FCSTD DOCUMENT  (FreeCAD 1.0R39109 (Git))
Label: base_platform
License: All rights reserved
LicenseURL: https://en.wikipedia.org/wiki/All_rights_reserved
objects: App::Link×27, App::FeaturePython×27, Assembly::JointGroup×1, Assembly::AssemblyObject×1
EXTERNAL_REF file=../parts_library/profile_40_serie.FCStd obj=Body001
EXTERNAL_REF file=../parts_library/profile_40_serie.FCStd obj=Body002
EXTERNAL_REF file=../parts_library/corner_bracket_40x40.FCStd obj=Part__Feature
EXTERNAL_REF file=../parts_library/profile_40_serie.FCStd obj=Body004

FEATURE [App::Link] profile_40x160x1350  label="profile_40x160x1350_right"
  LinkPlacement = pos=(605.692,0.000163098,162.079) rot=(0.57735,-0.57735,-0.57735;4.18879rad)
  LinkedObject = -> <external ../parts_library/profile_40_serie.FCStd>#Body001
  Placement = pos=(605.692,0.000163098,162.079) rot=(0.57735,-0.57735,-0.57735;4.18879rad)
FEATURE [App::Link] profile_40x160x1351  label="profile_40x160x1350_left"
  LinkPlacement = pos=(65.6922,3.43521e-05,162.079) rot=(0.57735,-0.57735,-0.57735;4.18879rad)
  LinkedObject = -> <external ../parts_library/profile_40_serie.FCStd>#Body001
  Placement = pos=(65.6922,3.43521e-05,162.079) rot=(0.57735,-0.57735,-0.57735;4.18879rad)
FEATURE [App::Link] profile_40x160x500  label="profile_40x160x500_front"
  LinkPlacement = pos=(540.393,744.701,-1.22589) rot=(0,-1,0;1.5708rad)
  LinkedObject = -> <external ../parts_library/profile_40_serie.FCStd>#Body002
  Placement = pos=(540.393,744.701,-1.22589) rot=(0,-1,0;1.5708rad)
FEATURE [App::Link] profile_40x160x1352  label="profile_40x160x500_rear"
  LinkPlacement = pos=(540.393,1284.7,-1.22602) rot=(0,-1,0;1.5708rad)
  LinkedObject = -> <external ../parts_library/profile_40_serie.FCStd>#Body002
  Placement = pos=(540.393,1284.7,-1.22602) rot=(0,-1,0;1.5708rad)
FEATURE [App::Link] corner_bracket_40x40  label="corner_bracket_40x40_000"
  LinkPlacement = pos=(-47.0395,846,140.426) rot=(0,0,-1;1.5708rad)
  LinkedObject = -> <external ../parts_library/corner_bracket_40x40.FCStd>#Part__Feature
  Placement = pos=(-47.0395,846,140.426) rot=(0,0,-1;1.5708rad)
FEATURE [App::Link] corner_bracket_40x041  label="corner_bracket_40x40_001"
  LinkPlacement = pos=(-47.0395,846,20.4265) rot=(0,0,-1;1.5708rad)
  LinkedObject = -> <external ../parts_library/corner_bracket_40x40.FCStd>#Part__Feature
  Placement = pos=(-47.0395,846,20.4265) rot=(0,0,-1;1.5708rad)
FEATURE [App::Link] corner_bracket_40x042  label="corner_bracket_40x40_002"
  LinkPlacement = pos=(-47.0396,1274,140.426) rot=(0.707107,0.707107,0;3.14159rad)
  LinkedObject = -> <external ../parts_library/corner_bracket_40x40.FCStd>#Part__Feature
  Placement = pos=(-47.0396,1274,140.426) rot=(0.707107,0.707107,0;3.14159rad)
FEATURE [App::Link] corner_bracket_40x043  label="corner_bracket_40x40_003"
  LinkPlacement = pos=(76.3929,1397.43,20.4263) rot=(0,0,1;3.14159rad)
  LinkedObject = -> <external ../parts_library/corner_bracket_40x40.FCStd>#Part__Feature
  Placement = pos=(76.3929,1397.43,20.4263) rot=(0,0,1;3.14159rad)
FEATURE [App::Link] corner_bracket_40x044  label="corner_bracket_40x40_004"
  LinkPlacement = pos=(504.393,722.568,140.426) rot=(-0.57735,0.57735,0.57735;0rad)
  LinkedObject = -> <external ../parts_library/corner_bracket_40x40.FCStd>#Part__Feature
  Placement = pos=(504.393,722.568,140.426) rot=(-0.57735,0.57735,0.57735;0rad)
FEATURE [App::Link] corner_bracket_40x045  label="corner_bracket_40x40_005"
  LinkPlacement = pos=(504.393,722.567,20.4264) rot=(-0.57735,0.57735,0.57735;0rad)
  LinkedObject = -> <external ../parts_library/corner_bracket_40x40.FCStd>#Part__Feature
  Placement = pos=(504.393,722.567,20.4264) rot=(-0.57735,0.57735,0.57735;0rad)
FEATURE [App::Link] corner_bracket_40x046  label="corner_bracket_40x40_006"
  LinkPlacement = pos=(627.826,1274,140.426) rot=(0,0,1;1.5708rad)
  LinkedObject = -> <external ../parts_library/corner_bracket_40x40.FCStd>#Part__Feature
  Placement = pos=(627.826,1274,140.426) rot=(0,0,1;1.5708rad)
FEATURE [App::Link] corner_bracket_40x047  label="corner_bracket_40x40_007"
  LinkPlacement = pos=(627.826,1274,20.4262) rot=(0,0,1;1.5708rad)
  LinkedObject = -> <external ../parts_library/corner_bracket_40x40.FCStd>#Part__Feature
  Placement = pos=(627.826,1274,20.4262) rot=(0,0,1;1.5708rad)
FEATURE [App::FeaturePython] GroundedJoint  label="GroundedJoint_profile_40x160x1350_left"  # Assembly grounded joint (typed FeaturePython)
  ObjectToGround = -> profile_40x160x1351
  Placement = pos=(65.6922,3.43521e-05,162.079) rot=(0.57735,-0.57735,-0.57735;4.18879rad)
FEATURE [App::FeaturePython] Joint  label="Fixed_profile_40x160x500_rear"  # Assembly joint (typed FeaturePython)
  Activated = true
  AngleMax = 0
  AngleMin = 0
  Detach1 = false
  Detach2 = false
  Distance = 0
  Distance2 = 0
  EnableAngleMax = false
  EnableAngleMin = false
  EnableLengthMax = false
  EnableLengthMin = false
  JointType = 0 (Fixed)
  LengthMax = 0
  LengthMin = 0
  Offset2 = pos=(0,0,0) rot=(0,0,-1;1.5708rad)
  Placement1 = pos=(3.65224,25.2989,1350) rot=(0.707107,0,0.707107;3.14159rad)
  Placement2 = pos=(159.652,65.2989,500) rot=(-0.57735,-0.57735,0.57735;2.0944rad)
  Reference1 = -> Assembly [profile_40x160x1351.Edge427,profile_40x160x1351.Vertex425]
  Reference2 = -> Assembly [profile_40x160x1352.Edge322,profile_40x160x1352.Vertex320]
FEATURE [App::FeaturePython] Joint001  label="Fixed_profile_40x160x1350_right"  # Assembly joint (typed FeaturePython)
  Activated = true
  AngleMax = 0
  AngleMin = 0
  Detach1 = false
  Detach2 = false
  Distance = 0
  Distance2 = 0
  EnableAngleMax = false
  EnableAngleMin = false
  EnableLengthMax = false
  EnableLengthMin = false
  JointType = 0 (Fixed)
  LengthMax = 0
  LengthMin = 0
  Offset2 = pos=(0,0,0) rot=(0,0,1;1.5708rad)
  Placement1 = pos=(159.652,65.2989,0) rot=(-0.707107,0,0.707107;3.14159rad)
  Placement2 = pos=(3.65224,65.2989,1350) rot=(-0.57735,0.57735,0.57735;4.18879rad)
  Reference1 = -> Assembly [profile_40x160x1352.Edge150,profile_40x160x1352.Vertex151]
  Reference2 = -> Assembly [profile_40x160x1350.Edge403,profile_40x160x1350.Vertex402]
FEATURE [App::FeaturePython] Joint002  label="Fixed_profile_40x160x500_front"  # Assembly joint (typed FeaturePython)
  Activated = true
  AngleMax = 0
  AngleMin = 0
  Detach1 = false
  Detach2 = false
  Distance = 0
  Distance2 = 0
  EnableAngleMax = false
  EnableAngleMin = false
  EnableLengthMax = false
  EnableLengthMin = false
  JointType = 0 (Fixed)
  LengthMax = 0
  LengthMin = 0
  Offset1 = pos=(0,-540,0) rot=(0,0,1;0rad)
  Offset2 = pos=(0,0,0) rot=(0,0,1;1.5708rad)
  Placement1 = pos=(159.652,605.299,500) rot=(-0.707107,0,0.707107;3.14159rad)
  Placement2 = pos=(3.65224,25.2989,1350) rot=(0.57735,-0.57735,0.57735;4.18879rad)
  Reference1 = -> Assembly [profile_40x160x500.Edge322,profile_40x160x500.Vertex320]
  Reference2 = -> Assembly [profile_40x160x1351.Edge427,profile_40x160x1351.Vertex425]
FEATURE [App::FeaturePython] Joint003  label="Fixed_corner_bracket_40x40_000"  # Assembly joint (typed FeaturePython)
  Activated = true
  AngleMax = 0
  AngleMin = 0
  Detach1 = false
  Detach2 = false
  Distance = 0
  Distance2 = 0
  EnableAngleMax = false
  EnableAngleMin = false
  EnableLengthMax = false
  EnableLengthMin = false
  JointType = 0 (Fixed)
  LengthMax = 0
  LengthMin = 0
  Offset2 = pos=(0,0,-1) rot=(0,0,1;3.14159rad)
  Placement1 = pos=(159.652,65.2989,500) rot=(0,1,0;3.14159rad)
  Placement2 = pos=(36,87.4326,18) rot=(0.57735,-0.57735,-0.57735;4.18879rad)
  Reference1 = -> Assembly [profile_40x160x500.Edge580,profile_40x160x500.Vertex320]
  Reference2 = -> Assembly [corner_bracket_40x40.Edge44,corner_bracket_40x40.Vertex43]
FEATURE [App::FeaturePython] Joint004  label="Fixed_corner_bracket_40x40_001"  # Assembly joint (typed FeaturePython)
  Activated = true
  AngleMax = 0
  AngleMin = 0
  Detach1 = false
  Detach2 = false
  Distance = 0
  Distance2 = 0
  EnableAngleMax = false
  EnableAngleMin = false
  EnableLengthMax = false
  EnableLengthMin = false
  JointType = 0 (Fixed)
  LengthMax = 0
  LengthMin = 0
  Offset2 = pos=(0,0,-1) rot=(0,0,1;3.14159rad)
  Placement1 = pos=(3.65224,65.2989,500) rot=(0,1,0;3.14159rad)
  Placement2 = pos=(36,87.4326,-18) rot=(0.57735,-0.57735,-0.57735;4.18879rad)
  Reference1 = -> Assembly [profile_40x160x500.Edge661,profile_40x160x500.Vertex401]
  Reference2 = -> Assembly [corner_bracket_40x041.Edge56,corner_bracket_40x041.Vertex54]
FEATURE [App::FeaturePython] Joint005  label="Fixed_corner_bracket_40x40_002"  # Assembly joint (typed FeaturePython)
  Activated = true
  AngleMax = 0
  AngleMin = 0
  Detach1 = false
  Detach2 = false
  Distance = 0
  Distance2 = 0
  EnableAngleMax = false
  EnableAngleMin = false
  EnableLengthMax = false
  EnableLengthMin = false
  JointType = 0 (Fixed)
  LengthMax = 0
  LengthMin = 0
  Offset2 = pos=(0,0,-1) rot=(0,0,1;0rad)
  Placement1 = pos=(159.652,25.2989,500) rot=(0,1,0;3.14159rad)
  Placement2 = pos=(36,87.4326,-18) rot=(0.57735,0.57735,0.57735;4.18879rad)
  Reference1 = -> Assembly [profile_40x160x1352.Edge557,profile_40x160x1352.Vertex297]
  Reference2 = -> Assembly [corner_bracket_40x042.Edge56,corner_bracket_40x042.Vertex54]
FEATURE [App::FeaturePython] Joint006  label="Fixed_corner_bracket_40x40_003"  # Assembly joint (typed FeaturePython)
  Activated = true
  AngleMax = 0
  AngleMin = 0
  Detach1 = false
  Detach2 = false
  Distance = 0
  Distance2 = 0
  EnableAngleMax = false
  EnableAngleMin = false
  EnableLengthMax = false
  EnableLengthMin = false
  JointType = 0 (Fixed)
  LengthMax = 0
  LengthMin = 0
  Offset2 = pos=(0,0,1) rot=(0,0,1;3.14159rad)
  Placement1 = pos=(35,87.4326,-18) rot=(0.707107,0,0.707107;3.14159rad)
  Placement2 = pos=(3.65224,25.2989,499) rot=(1,0,0;3.14159rad)
  Reference1 = -> Assembly [corner_bracket_40x043.Edge22,corner_bracket_40x043.Vertex22]
  Reference2 = -> Assembly [profile_40x160x1352.Edge684,profile_40x160x1352.Vertex424]
FEATURE [App::FeaturePython] Joint007  label="Fixed_corner_bracket_40x40_004"  # Assembly joint (typed FeaturePython)
  Activated = true
  AngleMax = 0
  AngleMin = 0
  Detach1 = false
  Detach2 = false
  Distance = 0
  Distance2 = 0
  EnableAngleMax = false
  EnableAngleMin = false
  EnableLengthMax = false
  EnableLengthMin = false
  JointType = 0 (Fixed)
  LengthMax = 0
  LengthMin = 0
  Offset2 = pos=(0,0,-1) rot=(0,0,1;3.14159rad)
  Placement1 = pos=(35,87.4326,18) rot=(0.707107,0,0.707107;3.14159rad)
  Placement2 = pos=(159.652,65.2989,1) rot=(1,0,0;3.14159rad)
  Reference1 = -> Assembly [corner_bracket_40x044.Edge7,corner_bracket_40x044.Vertex7]
  Reference2 = -> Assembly [profile_40x160x500.Edge580,profile_40x160x500.Vertex151]
FEATURE [App::FeaturePython] Joint008  label="Fixed_corner_bracket_40x40_005"  # Assembly joint (typed FeaturePython)
  Activated = true
  AngleMax = 0
  AngleMin = 0
  Detach1 = false
  Detach2 = false
  Distance = 0
  Distance2 = 0
  EnableAngleMax = false
  EnableAngleMin = false
  EnableLengthMax = false
  EnableLengthMin = false
  JointType = 0 (Fixed)
  LengthMax = 0
  LengthMin = 0
  Offset2 = pos=(0,0,1) rot=(0,0,1;3.14159rad)
  Placement1 = pos=(3.65224,65.2989,0) rot=(0,1,0;3.14159rad)
  Placement2 = pos=(36,87.4326,-18) rot=(0,-1,0;4.71239rad)
  Reference1 = -> Assembly [profile_40x160x500.Edge661,profile_40x160x500.Vertex70]
  Reference2 = -> Assembly [corner_bracket_40x045.Edge22,corner_bracket_40x045.Vertex22]
FEATURE [App::FeaturePython] Joint009  label="Fixed_corner_bracket_40x40_006"  # Assembly joint (typed FeaturePython)
  Activated = true
  AngleMax = 0
  AngleMin = 0
  Detach1 = false
  Detach2 = false
  Distance = 0
  Distance2 = 0
  EnableAngleMax = false
  EnableAngleMin = false
  EnableLengthMax = false
  EnableLengthMin = false
  JointType = 0 (Fixed)
  LengthMax = 0
  LengthMin = 0
  Offset2 = pos=(0,0,-1) rot=(0,0,1;3.14159rad)
  Placement1 = pos=(36,88.4326,18) rot=(0.57735,0.57735,0.57735;4.18879rad)
  Placement2 = pos=(159.652,25.2989,1) rot=(1,0,0;3.14159rad)
  Reference1 = -> Assembly [corner_bracket_40x046.Edge44,corner_bracket_40x046.Vertex43]
  Reference2 = -> Assembly [profile_40x160x1352.Edge557,profile_40x160x1352.Vertex174]
FEATURE [App::FeaturePython] Joint010  label="Fixed_corner_bracket_40x40_007"  # Assembly joint (typed FeaturePython)
  Activated = true
  AngleMax = 0
  AngleMin = 0
  Detach1 = false
  Detach2 = false
  Distance = 0
  Distance2 = 0
  EnableAngleMax = false
  EnableAngleMin = false
  EnableLengthMax = false
  EnableLengthMin = false
  JointType = 0 (Fixed)
  LengthMax = 0
  LengthMin = 0
  Offset2 = pos=(0,0,-1) rot=(0,0,1;3.14159rad)
  Placement1 = pos=(3.65224,25.2989,0) rot=(0,1,0;3.14159rad)
  Placement2 = pos=(36,87.4326,-18) rot=(0.57735,-0.57735,-0.57735;4.18879rad)
  Reference1 = -> Assembly [profile_40x160x1352.Edge684,profile_40x160x1352.Vertex47]
  Reference2 = -> Assembly [corner_bracket_40x047.Edge56,corner_bracket_40x047.Vertex54]
FEATURE [App::Link] profile_40x160x1353  label="profile_40x160x500_bottom"
  LinkPlacement = pos=(540.393,451.652,15.1275) rot=(0.57735,-0.57735,-0.57735;2.0944rad)
  LinkedObject = -> <external ../parts_library/profile_40_serie.FCStd>#Body002
  Placement = pos=(540.393,451.652,15.1275) rot=(0.57735,-0.57735,-0.57735;2.0944rad)
FEATURE [App::FeaturePython] Joint011  label="Fixed_profile_40x160x500_bottom"  # Assembly joint (typed FeaturePython)
  Activated = true
  AngleMax = 0
  AngleMin = 0
  Detach1 = false
  Detach2 = false
  Distance = 0
  Distance2 = 0
  EnableAngleMax = false
  EnableAngleMin = false
  EnableLengthMax = false
  EnableLengthMin = false
  JointType = 0 (Fixed)
  LengthMax = 0
  LengthMin = 0
  Offset2 = pos=(0,0,-290) rot=(0,0,1;1.5708rad)
  Placement1 = pos=(161.652,39.1989,1.137e-13) rot=(0,1,0;4.71239rad)
  Placement2 = pos=(107.752,65.2989,290) rot=(0.707107,0.707107,0;3.14159rad)
  Reference1 = -> Assembly [profile_40x160x1353.Face40,profile_40x160x1353.Vertex172]
  Reference2 = -> Assembly [profile_40x160x1350.Edge652,profile_40x160x1350.Vertex130]
FEATURE [App::Link] corner_bracket_40x048  label="corner_bracket_40x40_008"
  LinkPlacement = pos=(76.3932,377.433,60.4265) rot=(0,0,1;3.14159rad)
  LinkedObject = -> <external ../parts_library/corner_bracket_40x40.FCStd>#Part__Feature
  Placement = pos=(76.3932,377.433,60.4265) rot=(0,0,1;3.14159rad)
FEATURE [App::Link] corner_bracket_40x049  label="corner_bracket_40x40_009"
  LinkPlacement = pos=(-47.0394,430,4.42657) rot=(0.57735,0.57735,0.57735;4.18879rad)
  LinkedObject = -> <external ../parts_library/corner_bracket_40x40.FCStd>#Part__Feature
  Placement = pos=(-47.0394,430,4.42657) rot=(0.57735,0.57735,0.57735;4.18879rad)
FEATURE [App::Link] corner_bracket_40x050  label="corner_bracket_40x40_010"
  LinkPlacement = pos=(627.826,254,60.4264) rot=(0,0,1;1.5708rad)
  LinkedObject = -> <external ../parts_library/corner_bracket_40x40.FCStd>#Part__Feature
  Placement = pos=(627.826,254,60.4264) rot=(0,0,1;1.5708rad)
FEATURE [App::Link] corner_bracket_40x051  label="corner_bracket_40x40_011"
  LinkPlacement = pos=(627.826,430,4.42641) rot=(0.57735,-0.57735,0.57735;2.0944rad)
  LinkedObject = -> <external ../parts_library/corner_bracket_40x40.FCStd>#Part__Feature
  Placement = pos=(627.826,430,4.42641) rot=(0.57735,-0.57735,0.57735;2.0944rad)
FEATURE [App::FeaturePython] Joint012  label="Fixed_corner_bracket_40x40_008"  # Assembly joint (typed FeaturePython)
  Activated = true
  AngleMax = 0
  AngleMin = 0
  Detach1 = false
  Detach2 = false
  Distance = 0
  Distance2 = 0
  EnableAngleMax = false
  EnableAngleMin = false
  EnableLengthMax = false
  EnableLengthMin = false
  JointType = 0 (Fixed)
  LengthMax = 0
  LengthMin = 0
  Offset2 = pos=(0,0,1) rot=(0,0,1;1.5708rad)
  Placement1 = pos=(35,87.4326,18) rot=(0.707107,0,0.707107;3.14159rad)
  Placement2 = pos=(161.652,63.2989,499) rot=(0.707107,0.707107,0;3.14159rad)
  Reference1 = -> Assembly [corner_bracket_40x048.Edge7,corner_bracket_40x048.Vertex7]
  Reference2 = -> Assembly [profile_40x160x1353.Edge579,profile_40x160x1353.Vertex319]
FEATURE [App::FeaturePython] Joint013  label="Fixed_corner_bracket_40x40_009"  # Assembly joint (typed FeaturePython)
  Activated = true
  AngleMax = 0
  AngleMin = 0
  Detach1 = false
  Detach2 = false
  Distance = 0
  Distance2 = 0
  EnableAngleMax = false
  EnableAngleMin = false
  EnableLengthMax = false
  EnableLengthMin = false
  JointType = 0 (Fixed)
  LengthMax = 0
  LengthMin = 0
  Offset2 = pos=(0,0,-1) rot=(0,0,1;0rad)
  Placement1 = pos=(3.65224,25.2989,500) rot=(0,1,0;3.14159rad)
  Placement2 = pos=(36,87.4326,18) rot=(0.57735,0.57735,0.57735;4.18879rad)
  Reference1 = -> Assembly [profile_40x160x1353.Edge684,profile_40x160x1353.Vertex424]
  Reference2 = -> Assembly [corner_bracket_40x049.Edge44,corner_bracket_40x049.Vertex43]
FEATURE [App::FeaturePython] Joint014  label="Fixed_corner_bracket_40x40_010"  # Assembly joint (typed FeaturePython)
  Activated = true
  AngleMax = 0
  AngleMin = 0
  Detach1 = false
  Detach2 = false
  Distance = 0
  Distance2 = 0
  EnableAngleMax = false
  EnableAngleMin = false
  EnableLengthMax = false
  EnableLengthMin = false
  JointType = 0 (Fixed)
  LengthMax = 0
  LengthMin = 0
  Offset2 = pos=(0,0,-1) rot=(0,0,1;1.5708rad)
  Placement1 = pos=(36,88.4326,18) rot=(0.57735,0.57735,0.57735;4.18879rad)
  Placement2 = pos=(161.652,63.2989,1) rot=(0.707107,0.707107,0;3.14159rad)
  Reference1 = -> Assembly [corner_bracket_40x050.Edge44,corner_bracket_40x050.Vertex43]
  Reference2 = -> Assembly [profile_40x160x1353.Edge579,profile_40x160x1353.Vertex152]
FEATURE [App::FeaturePython] Joint015  label="Fixed_corner_bracket_40x40_011"  # Assembly joint (typed FeaturePython)
  Activated = true
  AngleMax = 0
  AngleMin = 0
  Detach1 = false
  Detach2 = false
  Distance = 0
  Distance2 = 0
  EnableAngleMax = false
  EnableAngleMin = false
  EnableLengthMax = false
  EnableLengthMin = false
  JointType = 0 (Fixed)
  LengthMax = 0
  LengthMin = 0
  Offset2 = pos=(0,0,-1) rot=(0,0,1;3.14159rad)
  Placement1 = pos=(3.65224,25.2989,0) rot=(0,1,0;3.14159rad)
  Placement2 = pos=(36,87.4326,-18) rot=(0.57735,-0.57735,-0.57735;4.18879rad)
  Reference1 = -> Assembly [profile_40x160x1353.Edge684,profile_40x160x1353.Vertex47]
  Reference2 = -> Assembly [corner_bracket_40x051.Edge56,corner_bracket_40x051.Vertex54]
FEATURE [App::Link] profile_40x120x780  label="profile_40x120x780_right"
  LinkPlacement = pos=(600.393,600,740.426) rot=(0,1,0;1.5708rad)
  LinkedObject = -> <external ../parts_library/profile_40_serie.FCStd>#Body004
  Placement = pos=(600.393,600,740.426) rot=(0,1,0;1.5708rad)
FEATURE [App::Link] profile_40x120x781  label="profile_40x120x780_left"
  LinkPlacement = pos=(-19.6069,600,40.4265) rot=(0,-1,0;1.5708rad)
  LinkedObject = -> <external ../parts_library/profile_40_serie.FCStd>#Body004
  Placement = pos=(-19.6069,600,40.4265) rot=(0,-1,0;1.5708rad)
FEATURE [App::Link] corner_bracket_40x052  label="corner_bracket_40x40_012"
  LinkPlacement = pos=(-35.6069,627.433,20.4265) rot=(1,0,0;3.14159rad)
  LinkedObject = -> <external ../parts_library/corner_bracket_40x40.FCStd>#Part__Feature
  Placement = pos=(-35.6069,627.433,20.4265) rot=(1,0,0;3.14159rad)
FEATURE [App::Link] corner_bracket_40x053  label="corner_bracket_40x40_013"
  LinkPlacement = pos=(-35.6068,627.433,140.427) rot=(1,0,0;3.14159rad)
  LinkedObject = -> <external ../parts_library/corner_bracket_40x40.FCStd>#Part__Feature
  Placement = pos=(-35.6068,627.433,140.427) rot=(1,0,0;3.14159rad)
FEATURE [App::Link] corner_bracket_40x054  label="corner_bracket_40x40_014"
  LinkPlacement = pos=(-35.6069,572.567,20.4265) rot=(0.57735,-0.57735,-0.57735;6.28318rad)
  LinkedObject = -> <external ../parts_library/corner_bracket_40x40.FCStd>#Part__Feature
  Placement = pos=(-35.6069,572.567,20.4265) rot=(0.57735,-0.57735,-0.57735;6.28318rad)
FEATURE [App::Link] corner_bracket_40x055  label="corner_bracket_40x40_015"
  LinkPlacement = pos=(-35.6068,572.567,140.427) rot=(0.57735,-0.57735,-0.57735;6.28318rad)
  LinkedObject = -> <external ../parts_library/corner_bracket_40x40.FCStd>#Part__Feature
  Placement = pos=(-35.6068,572.567,140.427) rot=(0.57735,-0.57735,-0.57735;6.28318rad)
FEATURE [App::Link] corner_bracket_40x056  label="corner_bracket_40x40_016"
  LinkPlacement = pos=(492.961,504,20.4264) rot=(-0.707107,-0.707107,0;3.14159rad)
  LinkedObject = -> <external ../parts_library/corner_bracket_40x40.FCStd>#Part__Feature
  Placement = pos=(492.961,504,20.4264) rot=(-0.707107,-0.707107,0;3.14159rad)
FEATURE [App::Link] corner_bracket_40x057  label="corner_bracket_40x40_017"
  LinkPlacement = pos=(492.961,504,140.426) rot=(-0.707107,-0.707107,0;3.14159rad)
  LinkedObject = -> <external ../parts_library/corner_bracket_40x40.FCStd>#Part__Feature
  Placement = pos=(492.961,504,140.426) rot=(-0.707107,-0.707107,0;3.14159rad)
FEATURE [App::Link] corner_bracket_40x058  label="corner_bracket_40x40_018"
  LinkPlacement = pos=(492.96,696,20.4264) rot=(0,0,1;4.71239rad)
  LinkedObject = -> <external ../parts_library/corner_bracket_40x40.FCStd>#Part__Feature
  Placement = pos=(492.96,696,20.4264) rot=(0,0,1;4.71239rad)
FEATURE [App::Link] corner_bracket_40x059  label="corner_bracket_40x40_019"
  LinkPlacement = pos=(616.393,572.568,140.426) rot=(0,-1,0;3.14159rad)
  LinkedObject = -> <external ../parts_library/corner_bracket_40x40.FCStd>#Part__Feature
  Placement = pos=(616.393,572.568,140.426) rot=(0,-1,0;3.14159rad)
FEATURE [App::FeaturePython] Joint016  label="Fixed_profile_40x120x780_left"  # Assembly joint (typed FeaturePython)
  Activated = true
  AngleMax = 0
  AngleMin = 0
  Detach1 = false
  Detach2 = false
  Distance = 0
  Distance2 = 0
  EnableAngleMax = false
  EnableAngleMin = false
  EnableLengthMax = false
  EnableLengthMin = false
  JointType = 0 (Fixed)
  LengthMax = 0
  LengthMin = 0
  Offset1 = pos=(-544.5,0,0) rot=(0,0,1;0rad)
  Offset2 = pos=(0,0,2) rot=(0,0,1;1.5708rad)
  Placement1 = pos=(159.652,65.2989,544.5) rot=(-0.707107,0,0.707107;3.14159rad)
  Placement2 = pos=(-38,-55.5,-20) rot=(0.57735,-0.57735,0.57735;4.18879rad)
  Reference1 = -> Assembly [profile_40x160x1351.Edge150,profile_40x160x1351.Vertex151]
  Reference2 = -> Assembly [profile_40x120x781.Edge949,profile_40x120x781.Vertex19]
FEATURE [App::FeaturePython] Joint017  label="Fixed_profile_40x120x780_right"  # Assembly joint (typed FeaturePython)
  Activated = true
  AngleMax = 0
  AngleMin = 0
  Detach1 = false
  Detach2 = false
  Distance = 0
  Distance2 = 0
  EnableAngleMax = false
  EnableAngleMin = false
  EnableLengthMax = false
  EnableLengthMin = false
  JointType = 0 (Fixed)
  LengthMax = 0
  LengthMin = 0
  Offset1 = pos=(544.5,0,0) rot=(0,0,1;0rad)
  Offset2 = pos=(0,0,-2) rot=(0,0,-1;1.5708rad)
  Placement1 = pos=(159.652,25.2989,544.5) rot=(0.707107,0,0.707107;3.14159rad)
  Placement2 = pos=(738,-55.5,-20) rot=(0.57735,0.57735,0.57735;2.0944rad)
  Reference1 = -> Assembly [profile_40x160x1350.Edge174,profile_40x160x1350.Vertex174]
  Reference2 = -> Assembly [profile_40x120x780.Edge949,profile_40x120x780.Vertex723]
FEATURE [App::FeaturePython] Joint018  label="Fixed_corner_bracket_40x40_012"  # Assembly joint (typed FeaturePython)
  Activated = true
  AngleMax = 0
  AngleMin = 0
  Detach1 = false
  Detach2 = false
  Distance = 0
  Distance2 = 0
  EnableAngleMax = false
  EnableAngleMin = false
  EnableLengthMax = false
  EnableLengthMin = false
  JointType = 0 (Fixed)
  LengthMax = 0
  LengthMin = 0
  Offset1 = pos=(2,0,0) rot=(0,0,1;0rad)
  Offset2 = pos=(0,0,-3.5) rot=(0,0,1;3.14159rad)
  Placement1 = pos=(-38,-60,-15.5) rot=(0,0,1;0rad)
  Placement2 = pos=(31.5,87.4326,18) rot=(0,-1,0;4.71239rad)
  Reference1 = -> Assembly [profile_40x120x781.Edge20,profile_40x120x781.Vertex20]
  Reference2 = -> Assembly [corner_bracket_40x052.Edge7,corner_bracket_40x052.Vertex7]
FEATURE [App::FeaturePython] Joint019  label="Fixed_corner_bracket_40x40_013"  # Assembly joint (typed FeaturePython)
  Activated = true
  AngleMax = 0
  AngleMin = 0
  Detach1 = false
  Detach2 = false
  Distance = 0
  Distance2 = 0
  EnableAngleMax = false
  EnableAngleMin = false
  EnableLengthMax = false
  EnableLengthMin = false
  JointType = 0 (Fixed)
  LengthMax = 0
  LengthMin = 0
  Offset1 = pos=(122,0,0) rot=(0,0,1;0rad)
  Offset2 = pos=(0,0,-3.5) rot=(0,0,1;3.14159rad)
  Placement1 = pos=(82,-60,-15.5) rot=(0,0,1;0rad)
  Placement2 = pos=(31.5,87.4326,18) rot=(0,-1,0;4.71239rad)
  Reference1 = -> Assembly [profile_40x120x781.Edge20,profile_40x120x781.Vertex20]
  Reference2 = -> Assembly [corner_bracket_40x053.Edge7,corner_bracket_40x053.Vertex7]
FEATURE [App::FeaturePython] Joint020  label="Fixed_corner_bracket_40x40_014"  # Assembly joint (typed FeaturePython)
  Activated = true
  AngleMax = 0
  AngleMin = 0
  Detach1 = false
  Detach2 = false
  Distance = 0
  Distance2 = 0
  EnableAngleMax = false
  EnableAngleMin = false
  EnableLengthMax = false
  EnableLengthMin = false
  JointType = 0 (Fixed)
  LengthMax = 0
  LengthMin = 0
  Offset1 = pos=(-2,0,0) rot=(0,0,1;0rad)
  Offset2 = pos=(0,0,-3.5) rot=(0,0,1;0rad)
  Placement1 = pos=(35,87.4326,-20) rot=(0.707107,0,0.707107;3.14159rad)
  Placement2 = pos=(-40,60,-19) rot=(0,0,1;0rad)
  Reference1 = -> Assembly [corner_bracket_40x054.Edge22,corner_bracket_40x054.Vertex22]
  Reference2 = -> Assembly [profile_40x120x781.Edge209,profile_40x120x781.Vertex210]
FEATURE [App::FeaturePython] Joint021  label="Fixed_corner_bracket_40x40_015"  # Assembly joint (typed FeaturePython)
  Activated = true
  AngleMax = 0
  AngleMin = 0
  Detach1 = false
  Detach2 = false
  Distance = 0
  Distance2 = 0
  EnableAngleMax = false
  EnableAngleMin = false
  EnableLengthMax = false
  EnableLengthMin = false
  JointType = 0 (Fixed)
  LengthMax = 0
  LengthMin = 0
  Offset1 = pos=(-122,0,0) rot=(0,0,1;0rad)
  Offset2 = pos=(0,0,-3.5) rot=(0,0,1;0rad)
  Placement1 = pos=(35,87.4326,-140) rot=(0.707107,0,0.707107;3.14159rad)
  Placement2 = pos=(-40,60,-19) rot=(0,0,1;0rad)
  Reference1 = -> Assembly [corner_bracket_40x055.Edge22,corner_bracket_40x055.Vertex22]
  Reference2 = -> Assembly [profile_40x120x781.Edge209,profile_40x120x781.Vertex210]
FEATURE [App::FeaturePython] Joint022  label="Fixed_corner_bracket_40x40_016"  # Assembly joint (typed FeaturePython)
  Activated = true
  AngleMax = 0
  AngleMin = 0
  Detach1 = false
  Detach2 = false
  Distance = 0
  Distance2 = 0
  EnableAngleMax = false
  EnableAngleMin = false
  EnableLengthMax = false
  EnableLengthMin = false
  JointType = 0 (Fixed)
  LengthMax = 0
  LengthMin = 0
  Offset1 = pos=(-2,0,0) rot=(0,0,1;0rad)
  Offset2 = pos=(0,0,3.5) rot=(0,0,1;0rad)
  Placement1 = pos=(738,-60,-15.5) rot=(0,0,1;0rad)
  Placement2 = pos=(36,91.9326,18) rot=(0.57735,0.57735,0.57735;4.18879rad)
  Reference1 = -> Assembly [profile_40x120x780.Edge742,profile_40x120x780.Vertex722]
  Reference2 = -> Assembly [corner_bracket_40x056.Edge44,corner_bracket_40x056.Vertex43]
FEATURE [App::FeaturePython] Joint023  label="Fixed_corner_bracket_40x40_017"  # Assembly joint (typed FeaturePython)
  Activated = true
  AngleMax = 0
  AngleMin = 0
  Detach1 = false
  Detach2 = false
  Distance = 0
  Distance2 = 0
  EnableAngleMax = false
  EnableAngleMin = false
  EnableLengthMax = false
  EnableLengthMin = false
  JointType = 0 (Fixed)
  LengthMax = 0
  LengthMin = 0
  Offset1 = pos=(-122,0,0) rot=(0,0,1;0rad)
  Offset2 = pos=(0,0,3.5) rot=(0,0,1;0rad)
  Placement1 = pos=(618,-60,-15.5) rot=(0,0,1;0rad)
  Placement2 = pos=(36,91.9326,18) rot=(0.57735,0.57735,0.57735;4.18879rad)
  Reference1 = -> Assembly [profile_40x120x780.Edge742,profile_40x120x780.Vertex722]
  Reference2 = -> Assembly [corner_bracket_40x057.Edge44,corner_bracket_40x057.Vertex43]
FEATURE [App::FeaturePython] Joint024  label="Fixed_corner_bracket_40x40_018"  # Assembly joint (typed FeaturePython)
  Activated = true
  AngleMax = 0
  AngleMin = 0
  Detach1 = false
  Detach2 = false
  Distance = 0
  Distance2 = 0
  EnableAngleMax = false
  EnableAngleMin = false
  EnableLengthMax = false
  EnableLengthMin = false
  JointType = 0 (Fixed)
  LengthMax = 0
  LengthMin = 0
  Offset1 = pos=(-2,0,0) rot=(0,0,1;0rad)
  Offset2 = pos=(0,0,3.5) rot=(0,0,1;3.14159rad)
  Placement1 = pos=(738,60,-15.5) rot=(0,0,1;0rad)
  Placement2 = pos=(36,91.9326,-18) rot=(0.57735,-0.57735,-0.57735;4.18879rad)
  Reference1 = -> Assembly [profile_40x120x780.Edge553,profile_40x120x780.Vertex532]
  Reference2 = -> Assembly [corner_bracket_40x058.Edge56,corner_bracket_40x058.Vertex54]
FEATURE [App::FeaturePython] Joint025  label="Fixed_corner_bracket_40x40_019"  # Assembly joint (typed FeaturePython)
  Activated = true
  AngleMax = 0
  AngleMin = 0
  Detach1 = false
  Detach2 = false
  Distance = 0
  Distance2 = 0
  EnableAngleMax = false
  EnableAngleMin = false
  EnableLengthMax = false
  EnableLengthMin = false
  JointType = 0 (Fixed)
  LengthMax = 0
  LengthMin = 0
  Offset1 = pos=(-122,0,0) rot=(0,0,1;0rad)
  Offset2 = pos=(0,0,-3.5) rot=(0,0,1;0rad)
  Placement1 = pos=(618,60,-15.5) rot=(0,0,1;0rad)
  Placement2 = pos=(31.5,87.4326,18) rot=(0.707107,0,0.707107;3.14159rad)
  Reference1 = -> Assembly [profile_40x120x780.Edge553,profile_40x120x780.Vertex532]
  Reference2 = -> Assembly [corner_bracket_40x059.Edge7,corner_bracket_40x059.Vertex7]
FEATURE [Assembly::JointGroup] Joints
  Group = -> [GroundedJoint,Joint,Joint001,Joint002,Joint003,Joint004,Joint005,Joint006,Joint007,Joint008,Joint009,Joint010,Joint011,Joint012,Joint013,Joint014,Joint015,Joint016,Joint017,Joint018,Joint019,Joint020,Joint021,Joint022,Joint023,Joint024,Joint025]
FEATURE [Assembly::AssemblyObject] Assembly  label="base_platform"
  Group = -> [Joints,profile_40x160x1350,profile_40x160x1351,profile_40x160x500,profile_40x160x1352,corner_bracket_40x40,corner_bracket_40x041,corner_bracket_40x042,corner_bracket_40x043,corner_bracket_40x044,corner_bracket_40x045,corner_bracket_40x046,corner_bracket_40x047,GroundedJoint,Joint,Joint001,Joint002,Joint003,Joint004,Joint005,Joint006,Joint007,Joint008,Joint009,Joint010,profile_40x160x1353,Joint011,+28 more]
  Origin = -> Origin
  Type = Assembly

RESOLVED EXTERNAL PARTS (link-assembly join: the EXTERNAL_REF files above that resolve inside this repo's crawl, each included once):
---- part ../parts_library/profile_40_serie.FCStd = doc fcstd_d02f419bdb3c ----
FCSTD DOCUMENT  (FreeCAD 1.0R39109 (Git))
Label: profile_40_serie
License: All rights reserved
LicenseURL: https://en.wikipedia.org/wiki/All_rights_reserved
objects: PartDesign::FeatureBase×6, PartDesign::Body×6, PartDesign::Pad×4, Part::Feature×3, PartDesign::Pocket×2
note: 39 computed .brp shape members not serialized (recipe doc carries the construction recipe); baked Part::Feature solids carry a one-line shape summary decoded from their .brp

FEATURE [Part::Feature] Part__Feature  label="profile_40x160x1000"
  shape: bbox 160 x 40 x 1000 mm, 262 faces (baked)
FEATURE [Part::Feature] Part__Feature003  label="profile_40x40x300"
  shape: bbox 40 x 40 x 300 mm, 147 faces (baked)
FEATURE [PartDesign::FeatureBase] BaseFeature
  BaseFeature = -> Part__Feature003
  Suppressed = false
FEATURE [PartDesign::Pad] Pad
  BaseFeature = -> BaseFeature
  Direction = (0,0,1)
  Length = 10
  Length2 = 10
  Profile = -> BaseFeature [Face147]
  Refine = true
  Suppressed = false
  Type = 0
FEATURE [PartDesign::Body] Body  label="profile_40x40x310"
  AllowCompound = false
  BaseFeature = -> Part__Feature003
  Group = -> [BaseFeature,Pad]
  Origin = -> Origin
  Tip = -> Pad
FEATURE [PartDesign::FeatureBase] BaseFeature001
  BaseFeature = -> Part__Feature
  Suppressed = false
FEATURE [PartDesign::Pad] Pad001
  BaseFeature = -> BaseFeature001
  Direction = (0,0,1)
  Length = 350
  Length2 = 10
  Profile = -> BaseFeature001 [Face9]
  Refine = true
  Suppressed = false
  Type = 0
FEATURE [PartDesign::Body] Body001  label="profile_40x160x1350"
  AllowCompound = false
  BaseFeature = -> Part__Feature
  Group = -> [BaseFeature001,Pad001]
  Origin = -> Origin001
  Tip = -> Pad001
FEATURE [PartDesign::FeatureBase] BaseFeature002
  BaseFeature = -> Part__Feature
  Suppressed = false
FEATURE [PartDesign::Pocket] Pocket
  BaseFeature = -> BaseFeature002
  Direction = (0,0,-1)
  Length = 500
  Length2 = 5
  Profile = -> BaseFeature002 [Face9]
  Refine = true
  Suppressed = false
  Type = 0
FEATURE [PartDesign::Body] Body002  label="profile_40x160x500"
  AllowCompound = false
  BaseFeature = -> Part__Feature
  Group = -> [BaseFeature002,Pocket]
  Origin = -> Origin002
  Tip = -> Pocket
FEATURE [PartDesign::FeatureBase] BaseFeature003
  BaseFeature = -> Part__Feature003
  Suppressed = false
FEATURE [PartDesign::Pad] Pad002
  BaseFeature = -> BaseFeature003
  Direction = (0,0,1)
  Length = 200
  Length2 = 10
  Profile = -> BaseFeature003 [Face147]
  Refine = true
  Suppressed = false
  Type = 0
FEATURE [PartDesign::Body] Body003  label="profile_40x40x500"
  AllowCompound = false
  BaseFeature = -> Part__Feature003
  Group = -> [BaseFeature003,Pad002]
  Origin = -> Origin003
  Tip = -> Pad002
FEATURE [Part::Feature] Part__Feature004  label="profile_40x120x80"
  shape: bbox 80 x 120 x 40 mm, 396 faces (baked)
FEATURE [PartDesign::FeatureBase] BaseFeature004
  BaseFeature = -> Part__Feature004
  Suppressed = false
FEATURE [PartDesign::Pad] Pad003
  BaseFeature = -> BaseFeature004
  Direction = (1,0,0)
  Length = 700
  Length2 = 10
  Profile = -> BaseFeature004 [Face396]
  Refine = true
  Suppressed = false
  Type = 0
FEATURE [PartDesign::Body] Body004  label="profile_40x120x780"
  AllowCompound = false
  BaseFeature = -> Part__Feature004
  Group = -> [BaseFeature004,Pad003]
  Origin = -> Origin004
  Tip = -> Pad003
FEATURE [PartDesign::FeatureBase] BaseFeature005
  BaseFeature = -> Part__Feature003
  Suppressed = false
FEATURE [PartDesign::Pocket] Pocket001
  BaseFeature = -> BaseFeature005
  Direction = (0,0,-1)
  Length = 30
  Length2 = 5
  Profile = -> BaseFeature005 [Face147]
  Refine = true
  Suppressed = false
  Type = 0
FEATURE [PartDesign::Body] Body005  label="profile_40x40x270"
  AllowCompound = false
  BaseFeature = -> Part__Feature003
  Group = -> [BaseFeature005,Pocket001]
  Origin = -> Origin005
  Tip = -> Pocket001
